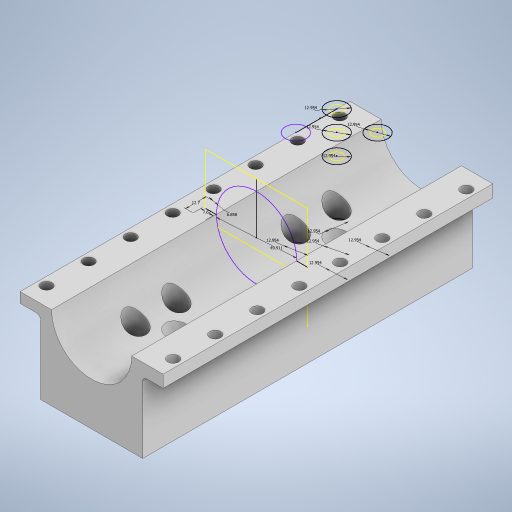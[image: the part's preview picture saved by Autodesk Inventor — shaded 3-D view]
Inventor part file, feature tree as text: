
AUTODESK INVENTOR PART (.ipt)
format: ipt  version: 2024.2 (Build 282272000, 272)  size: 494,080 bytes
history: native  units: in
note: dims shown in document units (in); Inventor stores cm internally (conversion verified against a paired STEP export)
features: extrude x10, sketch x10, pattern_linear x2, split x1, fillet x1, thicken_offset x1, mirror x1
ambient origin geometry x8: Origin, YZ Plane, XZ Plane, XY Plane, X Axis, Y Axis, Z Axis, Center Point
bodies: Solid1 (feature_tree)
feature tree (26):
  extrude  "Extrusion1"  Depth=4.0354in
  sketch  "Sketch2"  dims[d2=2.5in d3=0.0in d4=1.965in]
  extrude  "Extrusion2"  Depth=1.965in
  split  "Split1"
  extrude  "Extrusion3"  Depth=5.5in TaperAngle=0.0deg
  extrude  "Extrusion4"  Depth=0.5in
  sketch  "Sketch6"  dims[d11=1.0in d12=1.0in]
  sketch  "Sketch7"  dims[d13=0.27in d14=0.27in]
  extrude  "Extrusion5"  Depth=1.0in
  extrude  "Extrusion6"  Depth=0.27in
  sketch  "Sketch9"  dims[d17=0.27in]
  extrude  "Extrusion7"  Depth=0.27in
  pattern_linear  "Rectangular Pattern1"  Spacing1=0.51in  [1 undecoded]
  extrude  "Extrusion8"  Depth=4.0354in
  extrude  "Extrusion9"  Depth=4.0354in
  pattern_linear  "Rectangular Pattern2"  Spacing1=0.51in  [1 undecoded]
  fillet  "Fillet1"  Radius=0.51in
  thicken_offset  "Thicken1"
  extrude  "Extrusion10"  Depth=4.0354in
  mirror  "Mirror2"
  sketch  "Sketch1"  dims[d0=4.0354in d1=2.5in]
  sketch  "Sketch3"  dims[d5=5.5in d6=0.0in d7=5.5in d8=0.0in]
  sketch  "Sketch5"  dims[d9=0.5in d10=0.5in]
  sketch  "Sketch8"  dims[d15=0.27in d16=0.27in]
  sketch  "Sketch10"  dims[d18=5.5in d19=0.0in]
  sketch  "Sketch11"  dims[d20=0.51in d21=0.51in d22=0.51in d23=0.51in d24=0.51in d25=0.51in d26=0.51in d28=0.51in d29=0.51in d30=2.45in d31=0.0in d32=0.25in d33=0.5in d34=0.0in d35=0.3in d36=0.5in d37=0.27in d38=0.3in d39=0.0in d40=1.9685in d42=-1.0295in d43=0.3in d44=0.5in d45=0.0in d46=0.3in d47=0.5in d48=0.27in d49=0.5in d50=0.0in d51=1.9685in d53=1.0295in d54=0.1in d55=0.7874in d56=0.7874in d57=3.0in d58=0.0in d74=1.575in d75=4.0354in d76=4.0354in d59=0.5in d60=0.0344in]
note: 2 required parameter values undecoded (feature->parameter linkage not recoverable at this tier; creation-order binding heuristic only, values carry confidence <= 0.55)
